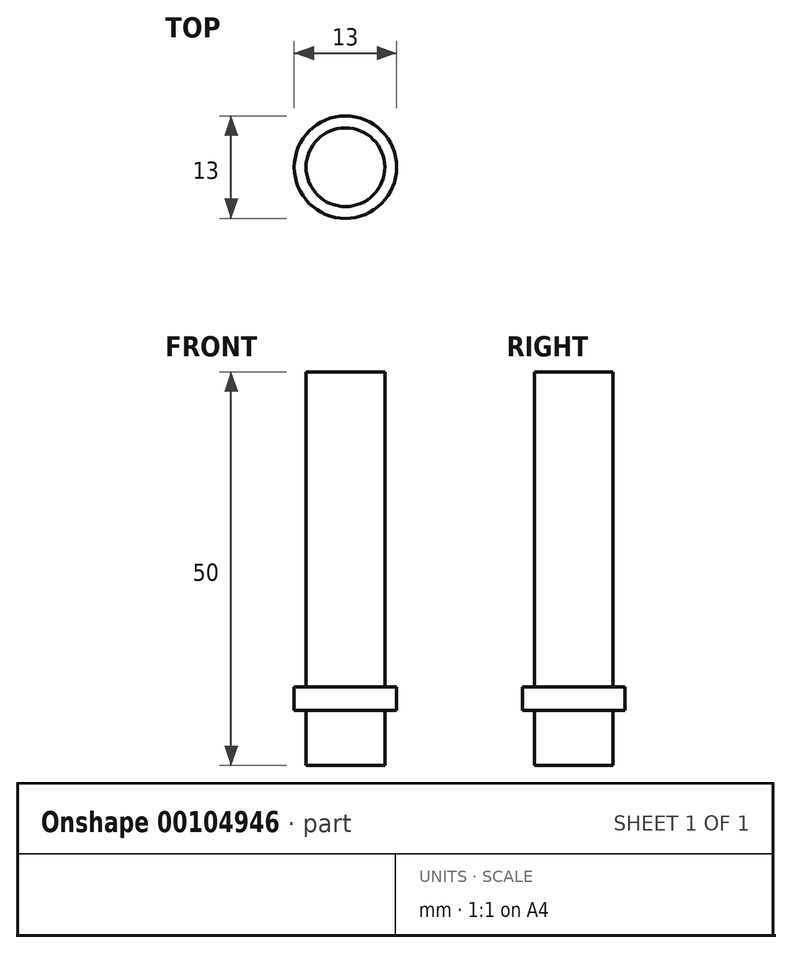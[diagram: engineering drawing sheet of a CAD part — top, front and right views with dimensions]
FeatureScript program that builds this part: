
annotation { "Feature Type Name" : "Feature", "Feature Type Description" : "" }
export const myFeature = defineFeature(function(context is Context, id is Id, definition is map)
    precondition{}
    {
        {
            var Q0;
            Q0=qCreatedBy(makeId("Front.planeOp"),FACE);
            var sketch = newSketch(context, id + "F0", { "sketchPlane" : qUnion([Q0])});
            skLineSegment(sketch, "E0", {"start": v(0, 0) * mm, "end": v(-5, 0) * mm});
            skLineSegment(sketch, "E1", {"start": v(-5, 0) * mm, "end": v(-5, 7) * mm});
            skLineSegment(sketch, "E2", {"start": v(-5, 7) * mm, "end": v(-6.5, 7) * mm});
            skLineSegment(sketch, "E3", {"start": v(-6.5, 7) * mm, "end": v(-6.5, 10) * mm});
            skLineSegment(sketch, "E4", {"start": v(-6.5, 10) * mm, "end": v(-5, 10) * mm});
            skLineSegment(sketch, "E5", {"start": v(-5, 10) * mm, "end": v(-5, 50) * mm});
            skLineSegment(sketch, "E6", {"start": v(-5, 50) * mm, "end": v(0, 50) * mm});
            skLineSegment(sketch, "E7", {"start": v(0, 50) * mm, "end": v(0, 0) * mm, "construction": true});
            skLineSegment(sketch, "E8", {"start": v(0, 50) * mm, "end": v(0, 0) * mm});
            skSolve(sketch);
        }
        {
            var Q0;
            Q0 = qSketchRegion(id + "F0", true);
            var Q1;
            Q1=sQuery(id+"F0.wireOp",EDGE,"E7");
            revolve(context, id + "F1", {"entities" : qUnion([Q0]), "axis" : qUnion([Q1]), "revolveType" : RevolveType.FULL});
        }
    });
